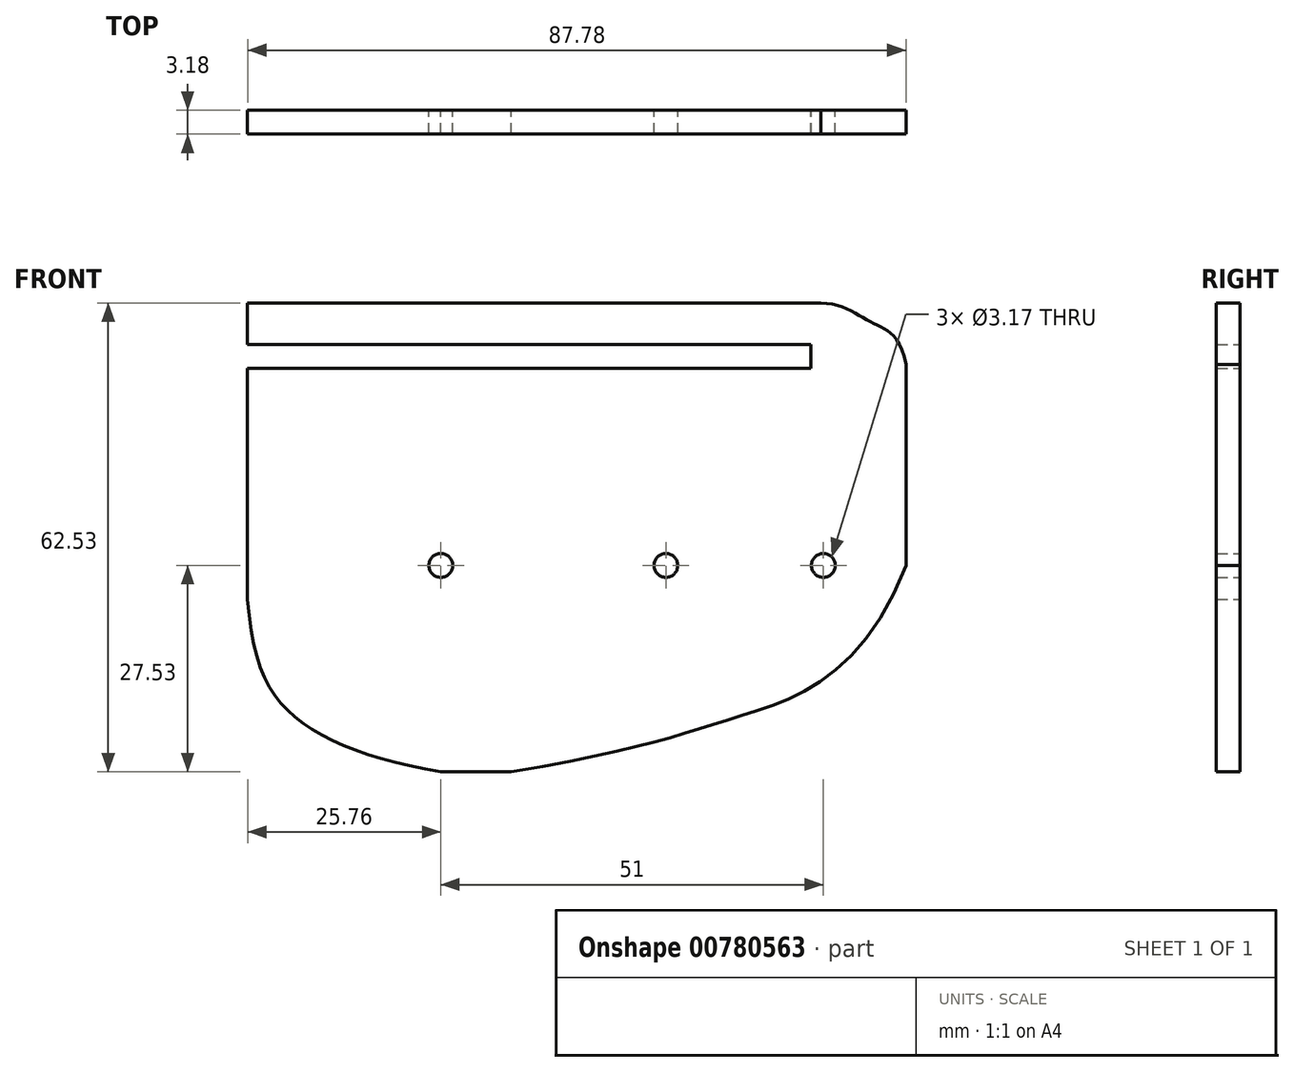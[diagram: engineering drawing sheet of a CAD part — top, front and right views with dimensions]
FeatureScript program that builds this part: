
annotation { "Feature Type Name" : "Feature", "Feature Type Description" : "" }
export const myFeature = defineFeature(function(context is Context, id is Id, definition is map)
    precondition{}
    {
        {
            var Q0;
            Q0=qCreatedBy(makeId("Front.planeOp"),FACE);
            var sketch = newSketch(context, id + "F0", { "sketchPlane" : qUnion([Q0])});
            skCircle(sketch, "E0", {"center": v(0, 0) * mm, "radius": 22.23 * mm});
            skCircle(sketch, "E1", {"center": v(30, 0) * mm, "radius": 9.53 * mm});
            skCircle(sketch, "E2", {"center": v(30, 0) * mm, "radius": 15.88 * mm});
            skCircle(sketch, "E3", {"center": v(51, 0) * mm, "radius": 6.35 * mm});
            skPoint(sketch, "E4", {"position": v(57.35, 0) * mm});
            skPoint(sketch, "E5", {"position": v(71.72, 0) * mm});
            skLineSegment(sketch, "E6.bottom", {"start": v(-25.76, 35) * mm, "end": v(50.65, 35) * mm});
            skLineSegment(sketch, "E6.top", {"start": v(0, -27.53) * mm, "end": v(9.4, -27.53) * mm});
            skLineSegment(sketch, "E6.left", {"start": v(-25.76, 35) * mm, "end": v(-25.76, 29.45) * mm});
            skLineSegment(sketch, "E6.right", {"start": v(62.02, 26.78) * mm, "end": v(62.02, 0) * mm});
            skLineSegment(sketch, "E7.bottom", {"start": v(-25.76, 29.45) * mm, "end": v(49.32, 29.45) * mm});
            skLineSegment(sketch, "E7.top", {"start": v(-25.76, 26.25) * mm, "end": v(49.32, 26.25) * mm});
            skLineSegment(sketch, "E7.right", {"start": v(49.32, 29.45) * mm, "end": v(49.32, 26.25) * mm});
            skPoint(sketch, "E8", {"position": v(49.32, 29.45) * mm});
            skFitSpline(sketch, "E9", {"points": [v(-25.76, -4.51) * mm, v(-19.56, -20.11) * mm, v(0, -27.53) * mm], "startDerivative": vector(4.05, -52) * mm, "endDerivative": vector(50.1, -8.83) * mm});
            skPoint(sketch, "E10.orphan", {"position": v(-25.76, -27.53) * mm});
            skFitSpline(sketch, "E11", {"points": [v(62.02, 0) * mm, v(39.08, -20.34) * mm, v(9.4, -27.53) * mm], "startDerivative": vector(-36.37, -93.4) * mm, "endDerivative": vector(-101.35, -17.1) * mm});
            skFitSpline(sketch, "E12", {"points": [v(50.65, 35) * mm, v(57.51, 32.36) * mm, v(62.02, 26.78) * mm], "startDerivative": vector(18.66, -0.65) * mm, "endDerivative": vector(5.83, -26.4) * mm});
            skLineSegment(sketch, "E13.trimOffspring", {"start": v(-25.76, 26.25) * mm, "end": v(-25.76, -4.51) * mm});
            skCircle(sketch, "E14", {"center": v(0, 0) * mm, "radius": 1.59 * mm});
            skCircle(sketch, "E15", {"center": v(30, 0) * mm, "radius": 1.59 * mm});
            skCircle(sketch, "E16", {"center": v(51, 0) * mm, "radius": 1.59 * mm});
            skSolve(sketch);
        }
        {
            var Q0;
            {var subQ4=sQuery(id+"F0.wireOp",EDGE,"E3");Q0=makeQuery(id+"F0.imprint","IMPRINT",FACE,{"disambiguationData":[TD([[makeQuery(id+"F0.imprint","IMPRINT",EDGE,{"derivedFrom":subQ4}),-1.0]])]});}
            var Q1;
            Q1=makeQuery(id+"F0.imprint","IMPRINT",FACE,{"disambiguationData":[TD([[makeQuery(id+"F0.imprint","IMPRINT",EDGE,{"derivedFrom":sQuery(id+"F0.wireOp",EDGE,"E1")}),1.0]])]});
            var Q2;
            {var subQ4=sQuery(id+"F0.wireOp",EDGE,"E1");Q2=makeQuery(id+"F0.imprint","IMPRINT",FACE,{"disambiguationData":[TD([[makeQuery(id+"F0.imprint","IMPRINT",EDGE,{"derivedFrom":subQ4}),-1.0]])]});}
            var Q3;
            Q3=makeQuery(id+"F0.imprint","IMPRINT",FACE,{"disambiguationData":[TD([[makeQuery(id+"F0.imprint","IMPRINT",EDGE,{"derivedFrom":sQuery(id+"F0.wireOp",EDGE,"E3")}),1.0]])]});
            var Q4;
            {var subQ0=sQuery(id+"F0.wireOp",EDGE,"E0");var subQ1=makeQuery(id+"F0.imprint","INTERSECT",VERTEX,{"derivedFrom":[subQ0,sQuery(id+"F0.wireOp",EDGE,"E1")]});Q4=makeQuery(id+"F0.imprint","IMPRINT",FACE,{"disambiguationData":[TD([[makeQuery(id+"F0.imprint","IMPRINT",EDGE,{"disambiguationData":[TD([[subQ1,-1.0]])],"derivedFrom":subQ0}),1.0]])]});}
            var Q5;
            Q5=makeQuery(id+"F0.imprint","IMPRINT",FACE,{"disambiguationData":[TD([[makeQuery(id+"F0.imprint","IMPRINT",EDGE,{"derivedFrom":sQuery(id+"F0.wireOp",EDGE,"E14")}),-1.0]])]});
            var Q6;
            Q6=makeQuery(id+"F0.imprint","IMPRINT",FACE,{"disambiguationData":[TD([[makeQuery(id+"F0.imprint","IMPRINT",EDGE,{"derivedFrom":sQuery(id+"F0.wireOp",EDGE,"E6.bottom")}),-1.0]])]});
            var Q7;
            Q7=makeQuery(id+"F0.imprint","IMPRINT",FACE,{"disambiguationData":[TD([[makeQuery(id+"F0.imprint","IMPRINT",EDGE,{"derivedFrom":sQuery(id+"F0.wireOp",EDGE,"E15")}),-1.0]])]});
            var Q8;
            Q8=makeQuery(id+"F0.imprint","IMPRINT",FACE,{"disambiguationData":[TD([[makeQuery(id+"F0.imprint","IMPRINT",EDGE,{"derivedFrom":sQuery(id+"F0.wireOp",EDGE,"E16")}),-1.0]])]});
            extrude(context, id + "F1", {"entities" : qUnion([Q0, Q1, Q2, Q3, Q4, Q5, Q6, Q7, Q8]), "depth" : 3.17 * mm, "offsetDistance" : 25.4 * mm});
        }
    });
